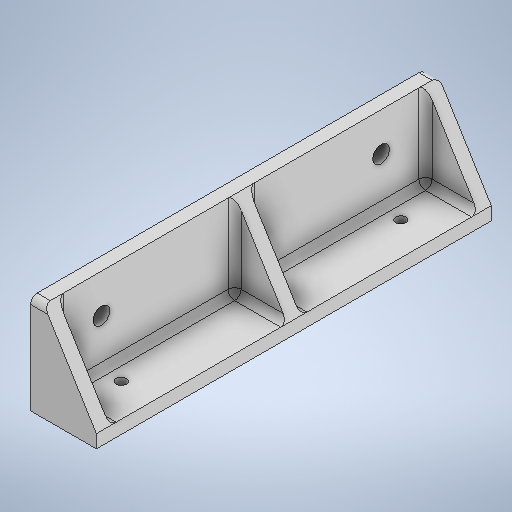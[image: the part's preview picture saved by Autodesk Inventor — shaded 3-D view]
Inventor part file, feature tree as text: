
AUTODESK INVENTOR PART (.ipt)
format: ipt  version: 2025 (Build 290162000, 162)  size: 320,000 bytes
history: native  units: in
note: dims shown in document units (in); Inventor stores cm internally (conversion verified against a paired STEP export)
features: sketch x5, extrude x3, fillet x2, hole x2, mirror x2, pattern_linear x1, plane x1
ambient origin geometry x8: Origin, YZ Plane, XZ Plane, XY Plane, X Axis, Y Axis, Z Axis, Center Point
bodies: Solid1 (feature_tree)
feature tree (16):
  extrude  "Extrusion1"  Depth=0.7874in
  extrude  "Extrusion2"  Depth=0.1575in
  pattern_linear  "Rectangular Pattern1"  Count1=12 Spacing1=0.0in
  fillet  "Fillet1"  Radius=0.1575in
  hole  "Hole1"  [1 undecoded]
  mirror  "Mirror1"
  hole  "Hole2"  [1 undecoded]
  mirror  "Mirror2"
  plane  "Work Plane1"
  extrude  "Extrusion3"  Depth=0.3937in
  fillet  "Fillet2"  Radius=1.6732in
  sketch  "Sketch1"  dims[d0=1.1811in d1=0.7874in]
  sketch  "Sketch2"  dims[d2=0.1575in d3=0.1575in d4=4.7244in d5=0.0in d6=0.1575in d7=0.0in]
  sketch  "Sketch3"  dims[d8=1.1811in d10=2.2835in d11=0.0787in]
  sketch  "Sketch4"  dims[d12=0.2008in d13=0.2362in d14=0.1575in d15=0.0787in d16=90.0deg d17=0.315in d18=0.8108in d19=0.7197in]
  sketch  "Sketch5"  dims[d20=1.6732in d21=0.122in d22=0.2362in d23=0.1575in d24=0.0787in d25=90.0deg d26=0.315in d27=0.8108in d28=0.3937in d29=1.6732in d30=-0.7197in d31=0.1378in d32=1.2205in d33=0.1378in d34=0.4724in d35=0.1181in d36=0.0in d37=0.0394in]
note: 2 required parameter values undecoded (feature->parameter linkage not recoverable at this tier; creation-order binding heuristic only, values carry confidence <= 0.55)
